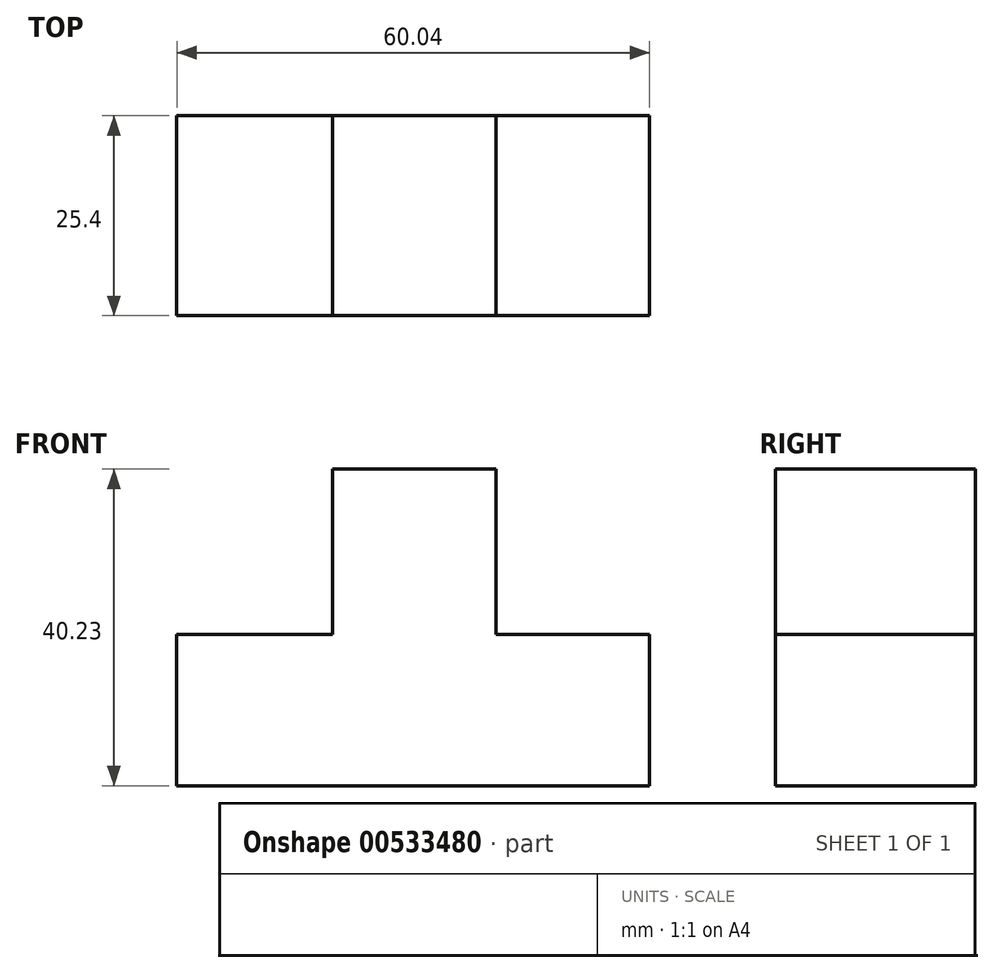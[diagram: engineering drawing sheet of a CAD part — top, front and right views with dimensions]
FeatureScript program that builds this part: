
annotation { "Feature Type Name" : "Feature", "Feature Type Description" : "" }
export const myFeature = defineFeature(function(context is Context, id is Id, definition is map)
    precondition{}
    {
        {
            var Q0;
            Q0=qCreatedBy(makeId("Front.planeOp"),FACE);
            var sketch = newSketch(context, id + "F0", { "sketchPlane" : qUnion([Q0])});
            skLineSegment(sketch, "E0", {"start": v(-14.63, 31.24) * mm, "end": v(6.1, 31.24) * mm});
            skLineSegment(sketch, "E1", {"start": v(6.1, 31.24) * mm, "end": v(6.1, 10.21) * mm});
            skLineSegment(sketch, "E2", {"start": v(6.1, 10.21) * mm, "end": v(6.1, 31.24) * mm});
            skLineSegment(sketch, "E3", {"start": v(-14.63, 31.24) * mm, "end": v(-14.63, 10.21) * mm});
            skLineSegment(sketch, "E4", {"start": v(-14.63, 10.21) * mm, "end": v(6.1, 10.21) * mm});
            skLineSegment(sketch, "E5", {"start": v(6.1, 10.21) * mm, "end": v(25.6, 10.21) * mm});
            skLineSegment(sketch, "E6", {"start": v(25.6, 10.21) * mm, "end": v(-14.63, 10.21) * mm});
            skLineSegment(sketch, "E7", {"start": v(-14.63, 10.21) * mm, "end": v(-34.44, 10.21) * mm});
            skLineSegment(sketch, "E8", {"start": v(-34.44, 10.21) * mm, "end": v(25.6, 10.21) * mm});
            skLineSegment(sketch, "E9", {"start": v(25.6, 10.21) * mm, "end": v(25.6, -9) * mm});
            skLineSegment(sketch, "E10", {"start": v(-34.44, -9) * mm, "end": v(25.6, -9) * mm});
            skLineSegment(sketch, "E11", {"start": v(-34.44, 10.21) * mm, "end": v(-34.44, -9) * mm});
            skSolve(sketch);
        }
        {
            var Q0;
            {var subQ0=sQuery(id+"F0.wireOp",EDGE,"E9");Q0=makeQuery(id+"F0.imprint","IMPRINT",FACE,{"disambiguationData":[TD([[makeQuery(id+"F0.imprint","IMPRINT",EDGE,{"derivedFrom":subQ0}),-1.0]])]});}
            var Q1;
            Q1=makeQuery(id+"F0.imprint","IMPRINT",FACE,{"disambiguationData":[TD([[makeQuery(id+"F0.imprint","IMPRINT",EDGE,{"derivedFrom":sQuery(id+"F0.wireOp",EDGE,"E0")}),-1.0]])]});
            extrude(context, id + "F1", {"entities" : qUnion([Q0, Q1]), "depth" : 25.4 * mm, "offsetDistance" : 25.4 * mm});
        }
    });
